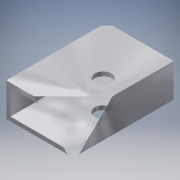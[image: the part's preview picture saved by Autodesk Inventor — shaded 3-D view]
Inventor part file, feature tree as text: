
AUTODESK INVENTOR PART (.ipt)
format: ipt  version: 2016 (Build 200138000, 138)  size: 116,224 bytes
history: native  units: in
note: dims shown in document units (in); Inventor stores cm internally (conversion verified against a paired STEP export)
features: sketch x2, extrude x1, hole x1
ambient origin geometry x8: Origin, YZ Plane, XZ Plane, XY Plane, X Axis, Y Axis, Z Axis, Center Point
bodies: Solid1 (feature_tree)
feature tree (4):
  extrude  "Extrusion1"  Depth=1.0in
  hole  "Hole1"  [1 undecoded]
  sketch  "Sketch1"  dims[d0=2.0in d1=1.0in]
  sketch  "Sketch2"  dims[d2=0.125in d3=3.0in d4=0.0in d6=1.5in d7=1.125in d8=0.75in d9=0.375in d10=0.25in d11=0.5635in d12=1.0in d13=0.8108in d14=1.0in]
note: 1 required parameter value undecoded (feature->parameter linkage not recoverable at this tier; creation-order binding heuristic only, values carry confidence <= 0.55)
